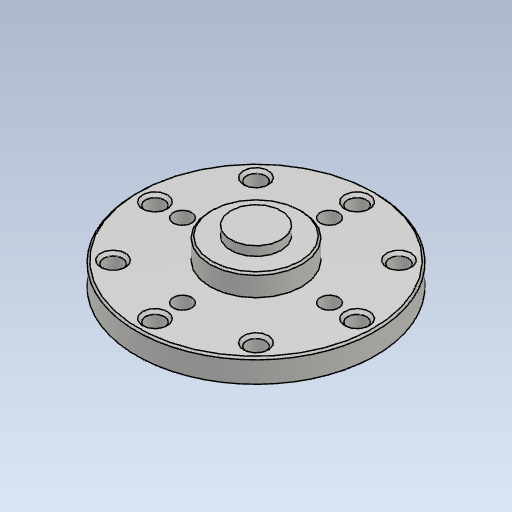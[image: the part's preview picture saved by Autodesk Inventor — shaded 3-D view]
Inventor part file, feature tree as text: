
AUTODESK INVENTOR PART (.ipt)
format: ipt  version: 2023 (Build 270158000, 158)  size: 360,960 bytes
history: native  units: mm
features: other x2, extrude x2, sketch x2, imported_body x1
ambient origin geometry x8: Origin, YZ Plane, XZ Plane, XY Plane, X Axis, Y Axis, Z Axis, Center Point
bodies: Body1 (feature_tree)
feature tree (7):
  other  "ソリッド1"
  other  "作業平面1"
  extrude  "押し出し1"  Depth=1.0mm
  extrude  "押し出し2"  Depth=10.0mm TaperAngle=0.0deg
  sketch  "スケッチ1"
  sketch  "スケッチ2"
  imported_body  "Base1"
